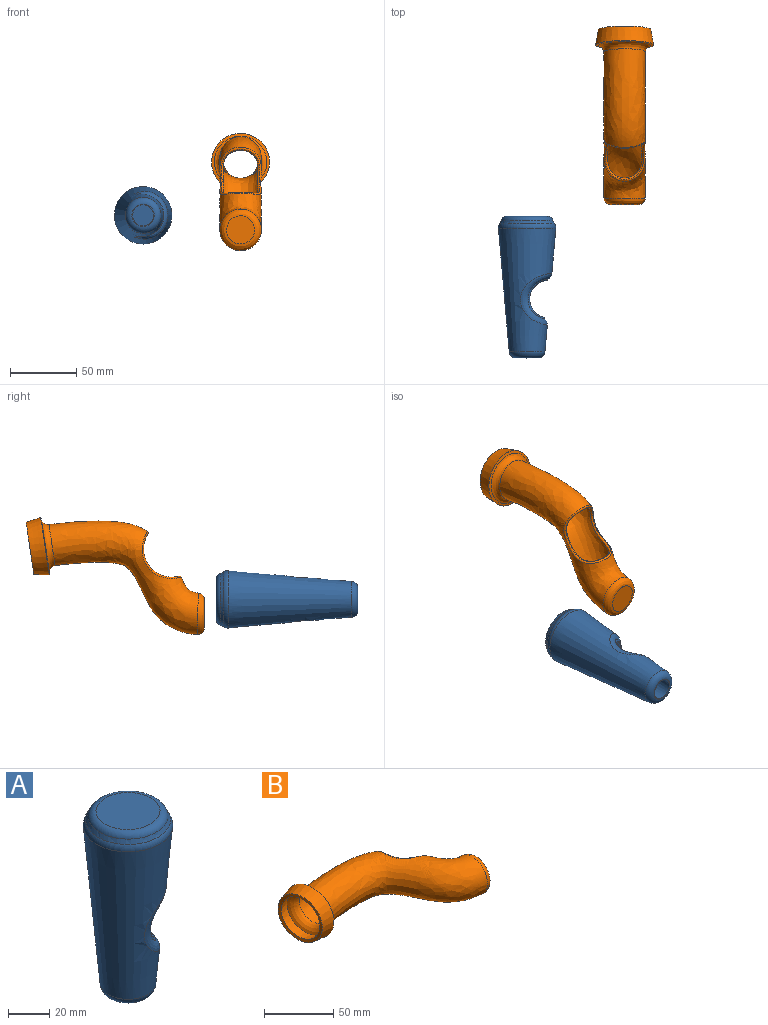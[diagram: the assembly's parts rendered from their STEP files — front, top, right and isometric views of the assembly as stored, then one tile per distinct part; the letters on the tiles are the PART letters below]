
ASSEMBLY  parts=2 mates=1
PART A: 13 faces, bbox 46.8x46.8x106.7 mm
  f0: cone r=7.98mm half-angle=5deg, axis (0,0,1), area 7316.5mm2, adj f1,f3,f4
  f1: plane 16.81x16.81mm, normal (0,0,-1), area 22.8mm2, adj f0,f9
  f2: plane 31.02x31.02mm, normal (0,0,-1), area 756mm2, adj f3
  f3: torus R=15.51mm, axis (0,0,1), area 244.6mm2, adj f0,f2
  f4: cylinder r=14.19mm len=27.75mm, axis (0,1,0), area 182.6mm2, adj f0,f5
  f5: bspline ~30.24x29.55mm, area 196.7mm2, adj f4,f11
  f6: cone r=13.04mm half-angle=5deg, axis (0,0,1), area 8273.2mm2, adj f9,f10,f11
  f7: plane 31.02x31.02mm, normal (0,0,1), area 756mm2, adj f8
  f8: torus R=15.51mm, axis (0,0,1), area 582.3mm2, adj f7,f12
  f9: torus R=8.4mm, axis (0,0,1), area 545.9mm2, adj f1,f6
  f10: torus R=16.55mm, axis (0,0,1), area 516.3mm2, adj f6,f12
  f11: bspline ~38.99x35.94mm, area 814mm2, adj f5,f6
  f12: bspline ~41.05x41.05mm, area 329.9mm2, adj f8,f10
PART B: 13 faces, bbox 134.3x88.7x43.7 mm
  f0: plane 21.14x21.05mm, normal (1,0,0), area 349.3mm2, adj f1
  f1: bspline ~31.66x31.23mm, area 685.8mm2, adj f0,f2
  f2: bspline ~114x85.56mm, area 11366mm2, adj f1,f3,f9
  f3: bspline ~39.61x39.18mm, area 762.4mm2, adj f2,f4
  f4: cone r=15.6mm half-angle=80deg, axis (-0.99,-0.15,0), area 276.8mm2, adj f3,f5
  f5: cone r=21.86mm half-angle=10deg, axis (0.99,0.15,0), area 1520.4mm2, adj f4,f6
  f6: cone r=13.59mm half-angle=80deg, axis (-0.99,-0.15,0), area 296.7mm2, adj f5,f7
  f7: cone r=19.36mm half-angle=10deg, axis (0.99,0.15,0), area 1034.2mm2, adj f6,f8
  f8: bspline ~37.85x37.45mm, area 969mm2, adj f7
  f9: bspline ~35.51x31.18mm, area 272.8mm2, adj f2,f10
  f10: bspline ~34.42x28.67mm, area 272.4mm2, adj f9
  f11: plane 21.14x21.05mm, normal (-1,0,0), area 349.3mm2, adj f12
  f12: bspline ~26.4x26.14mm, area 302.8mm2, adj f11
PLACE A rot(axis=(-1,0,0),90deg) t=(-62.48,-94.04,2.37)mm
PLACE B rot(axis=(0.58,-0.58,-0.58),120deg) t=(-49.33,21.5,33.16)mm
MATE parallel B.f0 <-> A.f0  axis (0,-1,0) through (-49.33,21.5,33.38)mm
